# Revit family: 3b948908-90ae-48af-a894-b6970f6c7e3a
name_source: partatom
category: Furniture
revit_build: Autodesk Revit 2016 (Build: 20161004_0715(x64)
units: mm (PartAtom-declared; Revit-internal decimal feet)

## family parameters
Always vertical = Yes
Cut with Voids When Loaded = No
OmniClass Number = 23.40.20.00
OmniClass Title = General Furniture and Specialties
Room Calculation Point = No
Shared = No
Work Plane-Based = No

## types (1)
- Standard
    Depth = 11"
    Description = SUICIDE RESISTANT ATTENDA 3 SHELF STORAGE
    Height = 57"
    Manufacturer = Behavioral Safety Products
    Manufacturer Fax = 706-705-1191
    Model = BF930
    Product Brochure URL = http://besafeprod.com
    Product Page URL = http://www.besafeprod.com
    Revit Object Download Link = http://library.smartbim.com
    Type Image = <None>
    URL = http://besafeprod.com
    Unit = Plastic - Behavioral Safety - Mulberry
    Width = 29"

## geometry (parser evidence)
native form markers: Sweep x6
no freeform markers — native parametric forms only
